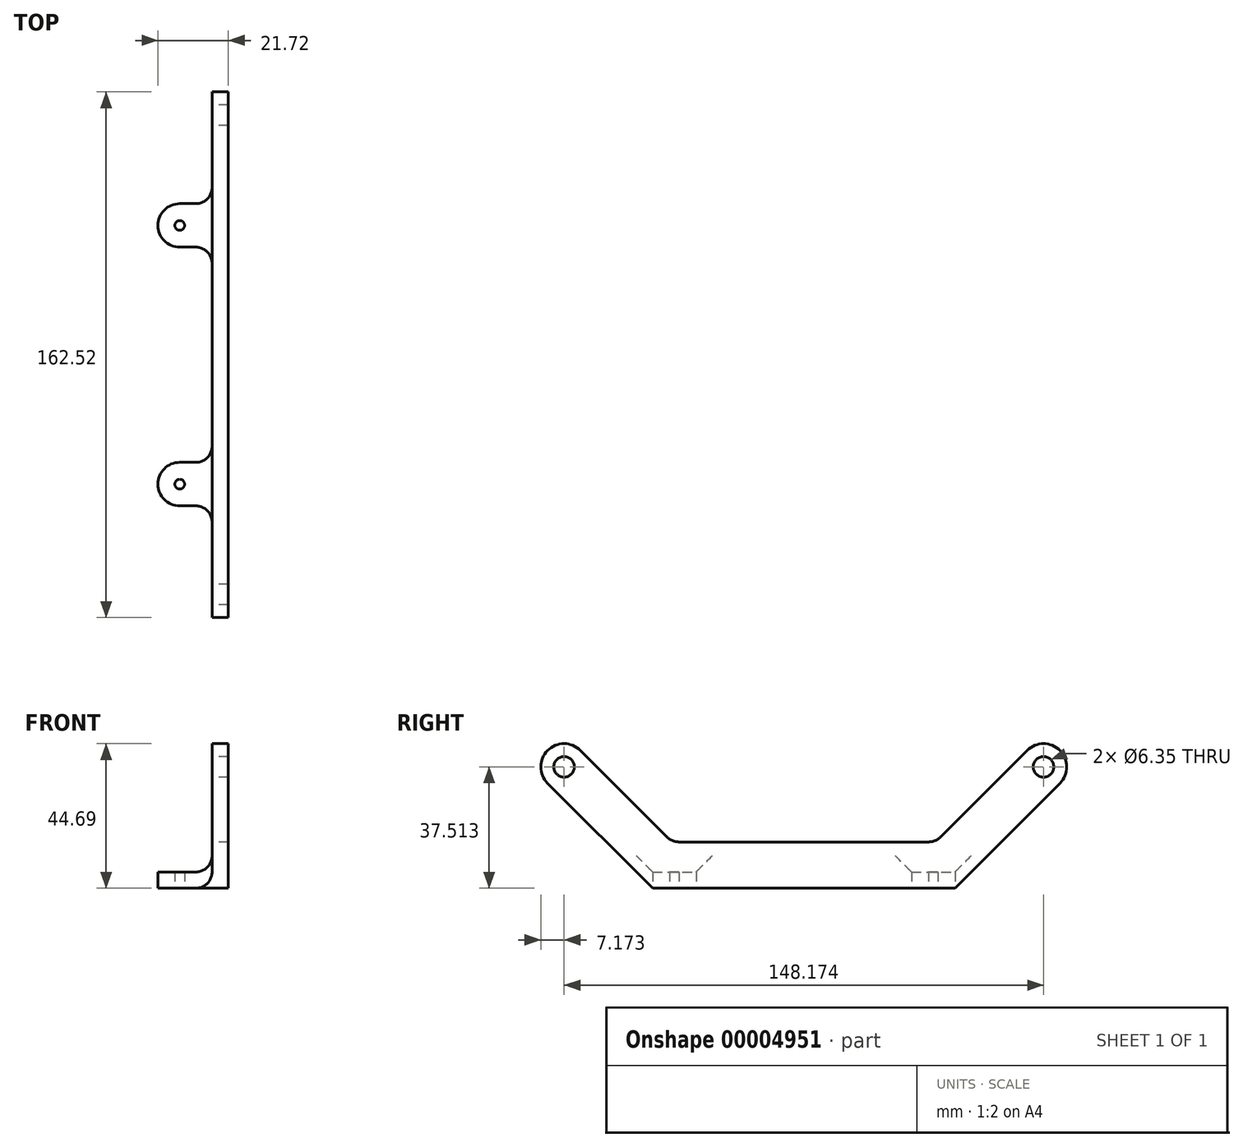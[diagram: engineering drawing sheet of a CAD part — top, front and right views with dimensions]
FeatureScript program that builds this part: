
annotation { "Feature Type Name" : "Feature", "Feature Type Description" : "" }
export const myFeature = defineFeature(function(context is Context, id is Id, definition is map)
    precondition{}
    {
        {
            var Q0;
            Q0=qCreatedBy(makeId("Right.planeOp"),FACE);
            var sketch = newSketch(context, id + "F0", { "sketchPlane" : qUnion([Q0])});
            skLineSegment(sketch, "E0", {"start": v(0, 0) * mm, "end": v(0, 37.51) * mm, "construction": true});
            skLineSegment(sketch, "E1", {"start": v(0, 37.51) * mm, "end": v(-74.09, 37.51) * mm, "construction": true});
            skCircle(sketch, "E2", {"center": v(-74.09, 37.51) * mm, "radius": 3.17 * mm});
            skCircle(sketch, "E3", {"center": v(0, 111.6) * mm, "radius": 101.6 * mm, "construction": true});
            skLineSegment(sketch, "E4", {"start": v(-74.09, 37.51) * mm, "end": v(0, 111.6) * mm, "construction": true});
            skPoint(sketch, "E5", {"position": v(0, 10) * mm});
            skLineSegment(sketch, "E6", {"start": v(-46.72, 0) * mm, "end": v(46.72, 0) * mm});
            skLineSegment(sketch, "E7", {"start": v(-46.72, 0) * mm, "end": v(-79.16, 32.44) * mm});
            skLineSegment(sketch, "E8", {"start": v(-69.01, 42.59) * mm, "end": v(-40.73, 14.3) * mm});
            skLineSegment(sketch, "E9", {"start": v(-74.09, 37.51) * mm, "end": v(-79.16, 32.44) * mm, "construction": true});
            skArc(sketch, "E10", {"start": v(-69.01, 42.59) * mm, "mid": v(-79.16, 42.59) * mm, "end": v(-79.16, 32.44) * mm});
            skLineSegment(sketch, "E11", {"start": v(-46.72, 0) * mm, "end": v(-40.73, 14.3) * mm, "construction": true});
            skLineSegment(sketch, "E12", {"start": v(-40.73, 14.3) * mm, "end": v(0, 111.6) * mm, "construction": true});
            skLineSegment(sketch, "E13.0.MirrorCS", {"start": v(46.72, 0) * mm, "end": v(79.16, 32.44) * mm});
            skCircle(sketch, "E13.1.MirrorC", {"center": v(74.09, 37.51) * mm, "radius": 3.17 * mm});
            skLineSegment(sketch, "E13.2.MirrorCS", {"start": v(69.01, 42.59) * mm, "end": v(40.73, 14.3) * mm});
            skArc(sketch, "E13.3.MirrorCS", {"start": v(69.01, 42.59) * mm, "mid": v(79.16, 42.59) * mm, "end": v(79.16, 32.44) * mm});
            skLineSegment(sketch, "E14", {"start": v(-40.73, 14.3) * mm, "end": v(40.73, 14.3) * mm});
            skSolve(sketch);
        }
        {
            var Q0;
            Q0 = qSketchRegion(id + "F0", true);
            extrude(context, id + "F1", {"entities" : qUnion([Q0]), "depth" : 5 * mm});
        }
        {
            var Q0;
            Q0=makeQuery(id+"F1.opExtrude","SWEPT_FACE",FACE,{"disambiguationData":[OSD([sQuery(id+"F0.wireOp",EDGE,"E6")])]});
            var sketch = newSketch(context, id + "F2", { "sketchPlane" : qUnion([Q0])});
            skLineSegment(sketch, "E15", {"start": v(5, -46.72) * mm, "end": v(-10, -46.72) * mm});
            skLineSegment(sketch, "E16", {"start": v(0, 0) * mm, "end": v(5, 0) * mm, "construction": true});
            skLineSegment(sketch, "E17", {"start": v(5, -33.28) * mm, "end": v(-10, -33.28) * mm});
            skLineSegment(sketch, "E18", {"start": v(-10, -46.72) * mm, "end": v(-10, -33.28) * mm, "construction": true});
            skCircle(sketch, "E19", {"center": v(-10, -40) * mm, "radius": 1.5 * mm});
            skArc(sketch, "E20", {"start": v(-10, -33.28) * mm, "mid": v(-16.72, -40) * mm, "end": v(-10, -46.72) * mm});
            skLineSegment(sketch, "E21", {"start": v(5, -46.72) * mm, "end": v(5, -33.28) * mm});
            skCircle(sketch, "E22.0.MirrorC", {"center": v(-10, 40) * mm, "radius": 1.5 * mm});
            skArc(sketch, "E22.1.MirrorCS", {"start": v(-10, 33.28) * mm, "mid": v(-16.72, 40) * mm, "end": v(-10, 46.72) * mm});
            skLineSegment(sketch, "E22.2.MirrorCS", {"start": v(5, 33.28) * mm, "end": v(-10, 33.28) * mm});
            skLineSegment(sketch, "E22.3.MirrorCS", {"start": v(5, 46.72) * mm, "end": v(5, 33.28) * mm});
            skLineSegment(sketch, "E22.4.MirrorCS", {"start": v(5, 46.72) * mm, "end": v(-10, 46.72) * mm});
            skSolve(sketch);
        }
        {
            var Q0;
            Q0 = qSketchRegion(id + "F2", true);
            extrude(context, id + "F3", {"entities" : qUnion([Q0]), "operationType" : NewBodyOperationType.ADD, "oppositeDirection" : true, "depth" : 5 * mm});
        }
        {
            var Q0;
            Q0=makeQuery(id+"F3.boolean.opBoolean","INTERSECT",EDGE,{"derivedFrom":[makeQuery(id+"F1.opExtrude","CAP_FACE",FACE,{"disambiguationData":[OSD([sQuery(id+"F0.wireOp",EDGE,"E2"),sQuery(id+"F0.wireOp",EDGE,"E6"),sQuery(id+"F0.wireOp",EDGE,"E7"),sQuery(id+"F0.wireOp",EDGE,"E8"),sQuery(id+"F0.wireOp",EDGE,"E10"),sQuery(id+"F0.wireOp",EDGE,"E13.0.MirrorCS"),sQuery(id+"F0.wireOp",EDGE,"E13.1.MirrorC"),sQuery(id+"F0.wireOp",EDGE,"E13.2.MirrorCS"),sQuery(id+"F0.wireOp",EDGE,"E13.3.MirrorCS"),sQuery(id+"F0.wireOp",EDGE,"E14")])],"isStart":true}),makeQuery(id+"F3.opExtrude","SWEPT_FACE",FACE,{"disambiguationData":[OSD([sQuery(id+"F2.wireOp",EDGE,"E17")])]})]});
            var Q1;
            Q1=makeQuery(id+"F3.boolean.opBoolean","INTERSECT",EDGE,{"derivedFrom":[makeQuery(id+"F1.opExtrude","CAP_FACE",FACE,{"disambiguationData":[OSD([sQuery(id+"F0.wireOp",EDGE,"E2"),sQuery(id+"F0.wireOp",EDGE,"E6"),sQuery(id+"F0.wireOp",EDGE,"E7"),sQuery(id+"F0.wireOp",EDGE,"E8"),sQuery(id+"F0.wireOp",EDGE,"E10"),sQuery(id+"F0.wireOp",EDGE,"E13.0.MirrorCS"),sQuery(id+"F0.wireOp",EDGE,"E13.1.MirrorC"),sQuery(id+"F0.wireOp",EDGE,"E13.2.MirrorCS"),sQuery(id+"F0.wireOp",EDGE,"E13.3.MirrorCS"),sQuery(id+"F0.wireOp",EDGE,"E14")])],"isStart":true}),makeQuery(id+"F3.opExtrude","SWEPT_FACE",FACE,{"disambiguationData":[OSD([sQuery(id+"F2.wireOp",EDGE,"E22.2.MirrorCS")])]})]});
            var Q2;
            Q2=makeQuery(id+"F1.opExtrude","SWEPT_EDGE",EDGE,{"disambiguationData":[OSD([sQuery(id+"F0.wireOp",EDGE,"E13.2.MirrorCS"),sQuery(id+"F0.wireOp",EDGE,"E14")])]});
            var Q3;
            Q3=makeQuery(id+"F1.opExtrude","SWEPT_EDGE",EDGE,{"disambiguationData":[OSD([sQuery(id+"F0.wireOp",EDGE,"E8"),sQuery(id+"F0.wireOp",EDGE,"E14")])]});
            var Q4;
            Q4=makeQuery(id+"F3.boolean.opBoolean","INTERSECT",EDGE,{"derivedFrom":[makeQuery(id+"F1.opExtrude","CAP_FACE",FACE,{"disambiguationData":[OSD([sQuery(id+"F0.wireOp",EDGE,"E2"),sQuery(id+"F0.wireOp",EDGE,"E6"),sQuery(id+"F0.wireOp",EDGE,"E7"),sQuery(id+"F0.wireOp",EDGE,"E8"),sQuery(id+"F0.wireOp",EDGE,"E10"),sQuery(id+"F0.wireOp",EDGE,"E13.0.MirrorCS"),sQuery(id+"F0.wireOp",EDGE,"E13.1.MirrorC"),sQuery(id+"F0.wireOp",EDGE,"E13.2.MirrorCS"),sQuery(id+"F0.wireOp",EDGE,"E13.3.MirrorCS"),sQuery(id+"F0.wireOp",EDGE,"E14")])],"isStart":true}),makeQuery(id+"F3.opExtrude","SWEPT_FACE",FACE,{"disambiguationData":[OSD([sQuery(id+"F2.wireOp",EDGE,"E15")])]})]});
            var Q5;
            Q5=makeQuery(id+"F3.boolean.opBoolean","INTERSECT",EDGE,{"derivedFrom":[makeQuery(id+"F1.opExtrude","CAP_FACE",FACE,{"disambiguationData":[OSD([sQuery(id+"F0.wireOp",EDGE,"E2"),sQuery(id+"F0.wireOp",EDGE,"E6"),sQuery(id+"F0.wireOp",EDGE,"E7"),sQuery(id+"F0.wireOp",EDGE,"E8"),sQuery(id+"F0.wireOp",EDGE,"E10"),sQuery(id+"F0.wireOp",EDGE,"E13.0.MirrorCS"),sQuery(id+"F0.wireOp",EDGE,"E13.1.MirrorC"),sQuery(id+"F0.wireOp",EDGE,"E13.2.MirrorCS"),sQuery(id+"F0.wireOp",EDGE,"E13.3.MirrorCS"),sQuery(id+"F0.wireOp",EDGE,"E14")])],"isStart":true}),makeQuery(id+"F3.opExtrude","SWEPT_FACE",FACE,{"disambiguationData":[OSD([sQuery(id+"F2.wireOp",EDGE,"E22.4.MirrorCS")])]})]});
            var Q6;
            Q6=makeQuery(id+"F3.boolean.opBoolean","INTERSECT",EDGE,{"derivedFrom":[makeQuery(id+"F1.opExtrude","CAP_FACE",FACE,{"disambiguationData":[OSD([sQuery(id+"F0.wireOp",EDGE,"E2"),sQuery(id+"F0.wireOp",EDGE,"E6"),sQuery(id+"F0.wireOp",EDGE,"E7"),sQuery(id+"F0.wireOp",EDGE,"E8"),sQuery(id+"F0.wireOp",EDGE,"E10"),sQuery(id+"F0.wireOp",EDGE,"E13.0.MirrorCS"),sQuery(id+"F0.wireOp",EDGE,"E13.1.MirrorC"),sQuery(id+"F0.wireOp",EDGE,"E13.2.MirrorCS"),sQuery(id+"F0.wireOp",EDGE,"E13.3.MirrorCS"),sQuery(id+"F0.wireOp",EDGE,"E14")])],"isStart":true}),makeQuery(id+"F3.opExtrude","CAP_FACE",FACE,{"disambiguationData":[OSD([sQuery(id+"F2.wireOp",EDGE,"E15"),sQuery(id+"F2.wireOp",EDGE,"E17"),sQuery(id+"F2.wireOp",EDGE,"E19"),sQuery(id+"F2.wireOp",EDGE,"E20"),sQuery(id+"F2.wireOp",EDGE,"E21")])],"isStart":false})]});
            var Q7;
            Q7=makeQuery(id+"F3.boolean.opBoolean","INTERSECT",EDGE,{"derivedFrom":[makeQuery(id+"F1.opExtrude","CAP_FACE",FACE,{"disambiguationData":[OSD([sQuery(id+"F0.wireOp",EDGE,"E2"),sQuery(id+"F0.wireOp",EDGE,"E6"),sQuery(id+"F0.wireOp",EDGE,"E7"),sQuery(id+"F0.wireOp",EDGE,"E8"),sQuery(id+"F0.wireOp",EDGE,"E10"),sQuery(id+"F0.wireOp",EDGE,"E13.0.MirrorCS"),sQuery(id+"F0.wireOp",EDGE,"E13.1.MirrorC"),sQuery(id+"F0.wireOp",EDGE,"E13.2.MirrorCS"),sQuery(id+"F0.wireOp",EDGE,"E13.3.MirrorCS"),sQuery(id+"F0.wireOp",EDGE,"E14")])],"isStart":true}),makeQuery(id+"F3.opExtrude","CAP_FACE",FACE,{"disambiguationData":[OSD([sQuery(id+"F2.wireOp",EDGE,"E22.0.MirrorC"),sQuery(id+"F2.wireOp",EDGE,"E22.1.MirrorCS"),sQuery(id+"F2.wireOp",EDGE,"E22.2.MirrorCS"),sQuery(id+"F2.wireOp",EDGE,"E22.3.MirrorCS"),sQuery(id+"F2.wireOp",EDGE,"E22.4.MirrorCS")])],"isStart":false})]});
            fillet(context, id + "F4", {"entities" : qUnion([Q0, Q1, Q2, Q3, Q4, Q5, Q6, Q7]), "radius" : 5 * mm, "tangentPropagation" : true, "allowEdgeOverflow" : false});
        }
    });
